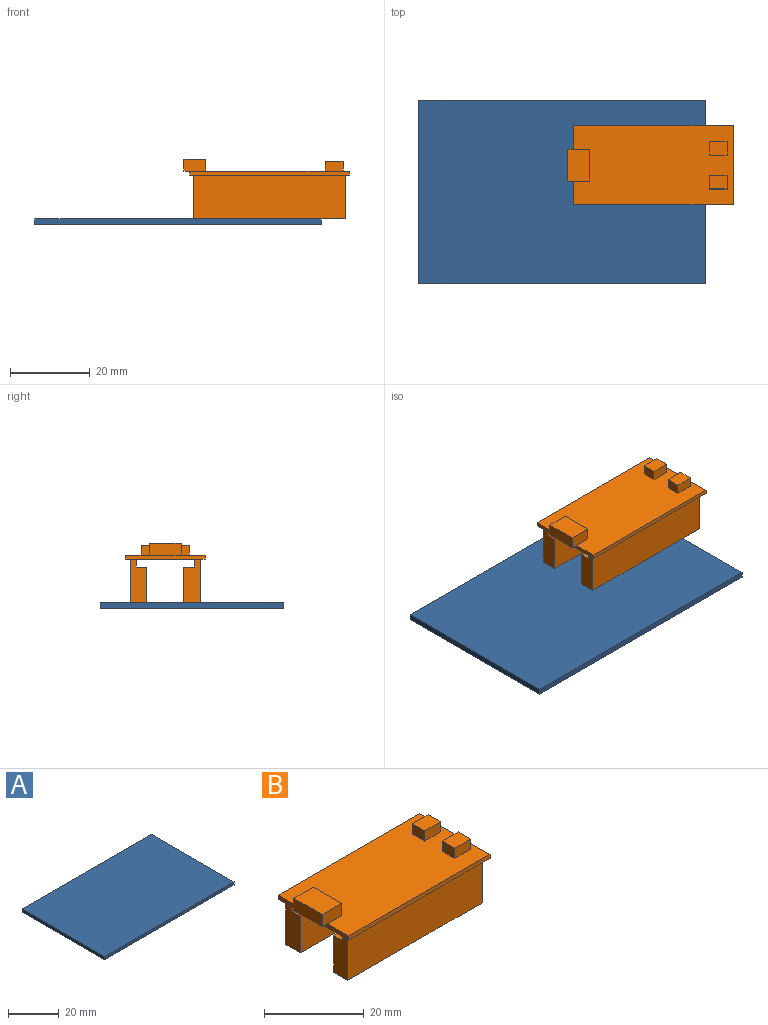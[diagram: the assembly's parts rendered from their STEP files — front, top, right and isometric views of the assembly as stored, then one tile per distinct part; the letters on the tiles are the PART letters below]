
ASSEMBLY  parts=2 mates=1
PART A: 6 faces, bbox 72x46x1.5 mm
  f0: plane 46x1.5mm, normal (1,0,0), area 69mm2, adj f1,f3,f4,f5
  f1: plane 72x1.5mm, normal (0,1,0), area 108mm2, adj f0,f2,f4,f5
  f2: plane 46x1.5mm, normal (-1,0,0), area 69mm2, adj f1,f3,f4,f5
  f3: plane 72x1.5mm, normal (0,-1,0), area 108mm2, adj f0,f2,f4,f5
  f4: plane 72x46mm, normal (0,0,1), area 3312mm2, adj f0,f1,f2,f3
  f5: plane 72x46mm, normal (0,0,-1), area 3312mm2, adj f0,f1,f2,f3
PART B: 36 faces, bbox 41.5x20x15 mm
  f0: plane 40x20mm, normal (0,0,1), area 736.5mm2, adj f1,f2,f3,f4,f6,f7,f8,f12
  f1: plane 40x1mm, normal (0,-1,0), area 40mm2, adj f0,f2,f4,f5
  f2: plane 20x1mm, normal (1,0,0), area 20mm2, adj f0,f1,f3,f5
  f3: plane 40x1mm, normal (0,1,0), area 40mm2, adj f0,f2,f4,f5
  f4: plane 20x1mm, normal (-1,0,0), area 20mm2, adj f0,f1,f3,f5,f11
  f5: plane 40x20mm, normal (0,0,-1), area 686mm2, adj f1,f2,f3,f4,f22,f23,f24,f25
  f6: plane 5.5x3mm, normal (0,-1,0), area 16.5mm2, adj f0,f7,f9,f10,f11
  f7: plane 8x3mm, normal (1,0,0), area 24mm2, adj f0,f6,f8,f10
  f8: plane 5.5x3mm, normal (0,1,0), area 16.5mm2, adj f0,f7,f9,f10,f11
  f9: plane 8x3mm, normal (-1,0,0), area 24mm2, adj f6,f8,f10,f11
  f10: plane 8x5.5mm, normal (0,0,1), area 44mm2, adj f6,f7,f8,f9
  f11: plane 8x1.5mm, normal (0,0,-1), area 12mm2, adj f4,f6,f8,f9
  f12: plane 4.5x2.5mm, normal (0,-1,0), area 11.2mm2, adj f0,f13,f15,f16
  f13: plane 3.5x2.5mm, normal (1,0,0), area 8.8mm2, adj f0,f12,f14,f16
  f14: plane 4.5x2.5mm, normal (0,1,0), area 11.2mm2, adj f0,f13,f15,f16
  f15: plane 3.5x2.5mm, normal (-1,0,0), area 8.8mm2, adj f0,f12,f14,f16
  f16: plane 4.5x3.5mm, normal (0,0,1), area 15.7mm2, adj f12,f13,f14,f15
  f17: plane 4.5x2.5mm, normal (0,1,0), area 11.2mm2, adj f0,f18,f20,f21
  f18: plane 3.5x2.5mm, normal (-1,0,0), area 8.8mm2, adj f0,f17,f19,f21
  f19: plane 4.5x2.5mm, normal (0,-1,0), area 11.2mm2, adj f0,f18,f20,f21
  f20: plane 3.5x2.5mm, normal (1,0,0), area 8.8mm2, adj f0,f17,f19,f21
  f21: plane 4.5x3.5mm, normal (0,0,1), area 15.7mm2, adj f17,f18,f19,f20
  f22: plane 38x2mm, normal (0,-1,0), area 76mm2, adj f5,f23,f25,f32
  f23: plane 11x4.04mm, normal (-1,0,0), area 39.4mm2, adj f5,f22,f24,f30,f31,f32
  f24: plane 38x11mm, normal (0,1,0), area 418mm2, adj f5,f23,f25,f31
  f25: plane 11x4.04mm, normal (1,0,0), area 39.4mm2, adj f5,f22,f24,f30,f31,f32
  f26: plane 11x4.04mm, normal (-1,0,0), area 39.4mm2, adj f5,f27,f29,f33,f34,f35
  f27: plane 38x2mm, normal (0,1,0), area 76mm2, adj f5,f26,f28,f33
  f28: plane 11x4.04mm, normal (1,0,0), area 39.4mm2, adj f5,f27,f29,f33,f34,f35
  f29: plane 38x11mm, normal (0,-1,0), area 418mm2, adj f5,f26,f28,f35
  f30: plane 38x9mm, normal (0,-1,0), area 342mm2, adj f23,f25,f31,f32
  f31: plane 38x4.04mm, normal (0,0,-1), area 153.5mm2, adj f23,f24,f25,f30
  f32: plane 38x2.54mm, normal (0,0,1), area 96.5mm2, adj f22,f23,f25,f30
  f33: plane 38x2.54mm, normal (0,0,1), area 96.5mm2, adj f26,f27,f28,f34
  f34: plane 38x9mm, normal (0,1,0), area 342mm2, adj f26,f28,f33,f35
  f35: plane 38x4.04mm, normal (0,0,-1), area 153.5mm2, adj f26,f28,f29,f34
PLACE A at identity fixed
PLACE B t=(22.94,6.73,12.5)mm
MATE planar B.f35 <-> A.f4  axis (0,0,-1) through (22.94,0,1.5)mm
